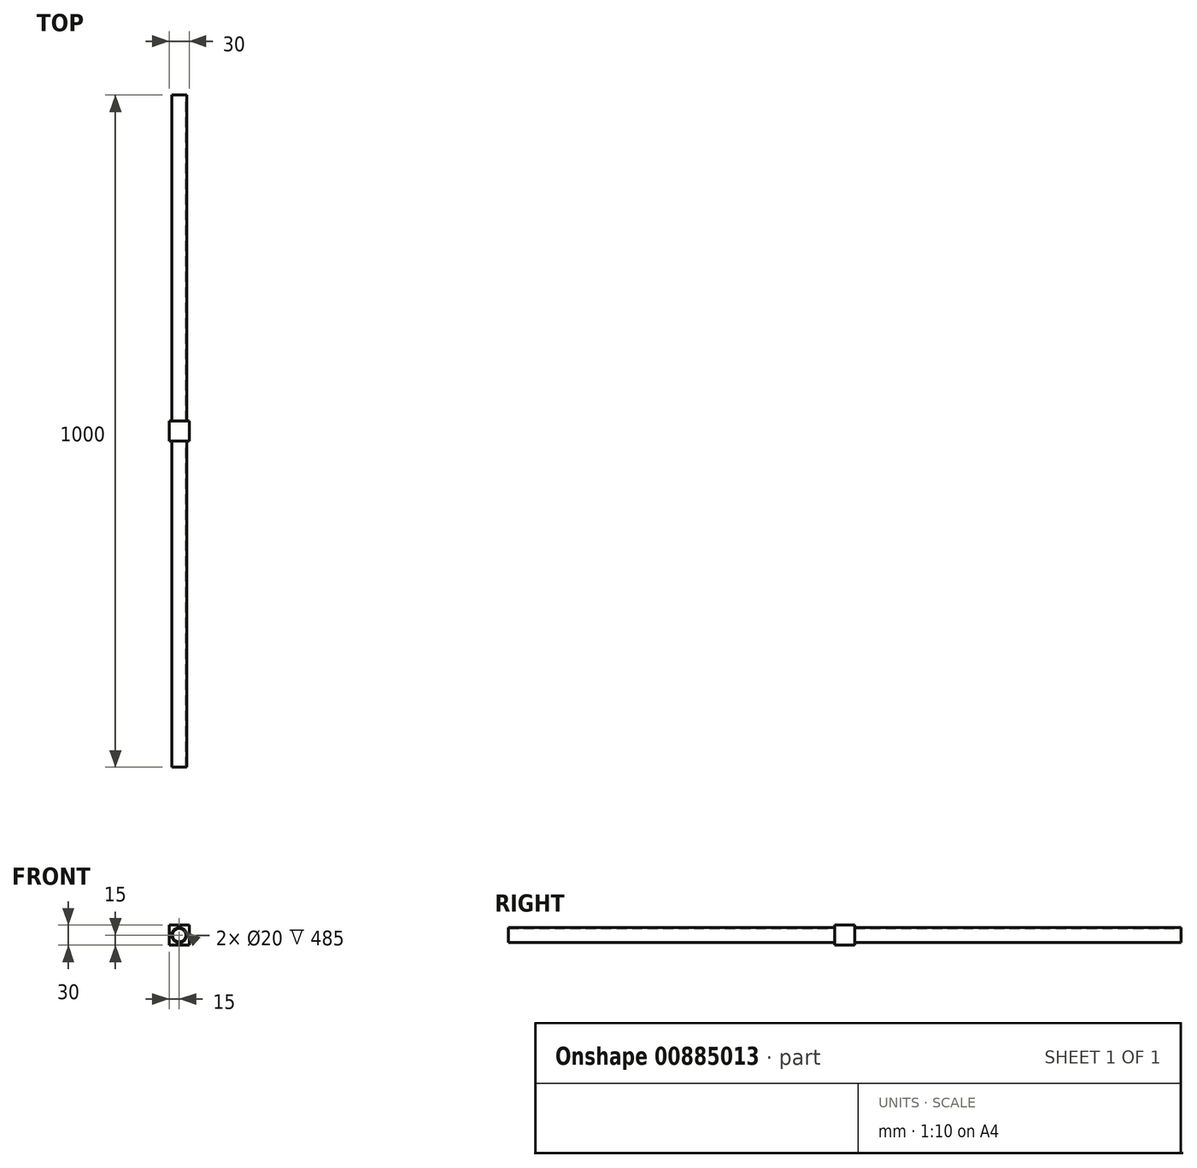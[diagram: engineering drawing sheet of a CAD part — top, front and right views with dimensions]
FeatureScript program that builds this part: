
annotation { "Feature Type Name" : "Feature", "Feature Type Description" : "" }
export const myFeature = defineFeature(function(context is Context, id is Id, definition is map)
    precondition{}
    {
        {
            var Q0;
            Q0=qCreatedBy(makeId("Front.planeOp"),FACE);
            var sketch = newSketch(context, id + "F0", { "sketchPlane" : qUnion([Q0])});
            skCircle(sketch, "E0", {"center": v(0, 0) * mm, "radius": 10 * mm});
            skCircle(sketch, "E1", {"center": v(0, 0) * mm, "radius": 11 * mm});
            skSolve(sketch);
        }
        {
            var Q0;
            Q0 = qSketchRegion(id + "F0", true);
            extrude(context, id + "F1", {"entities" : qUnion([Q0]), "depth" : 1000 * mm, "offsetDistance" : 25.4 * mm});
        }
        {
            var Q0;
            Q0=qCreatedBy(makeId("Top.planeOp"),FACE);
            var sketch = newSketch(context, id + "F2", { "sketchPlane" : qUnion([Q0])});
            skLineSegment(sketch, "E2", {"start": v(0, 0) * mm, "end": v(0, -500) * mm});
            skLineSegment(sketch, "E3.bottom", {"start": v(15, -515) * mm, "end": v(-15, -515) * mm});
            skLineSegment(sketch, "E3.top", {"start": v(15, -485) * mm, "end": v(-15, -485) * mm});
            skLineSegment(sketch, "E3.left", {"start": v(15, -515) * mm, "end": v(15, -485) * mm});
            skLineSegment(sketch, "E3.right", {"start": v(-15, -515) * mm, "end": v(-15, -485) * mm});
            skPoint(sketch, "E3.middle", {"position": v(0, -500) * mm});
            skSolve(sketch);
        }
        {
            var Q0;
            Q0 = qSketchRegion(id + "F2", true);
            extrude(context, id + "F3", {"entities" : qUnion([Q0]), "operationType" : NewBodyOperationType.ADD, "depth" : 15 * mm, "offsetDistance" : 25.4 * mm, "hasSecondDirection" : true, "secondDirectionOppositeDirection" : true, "secondDirectionDepth" : 15 * mm});
        }
    });
